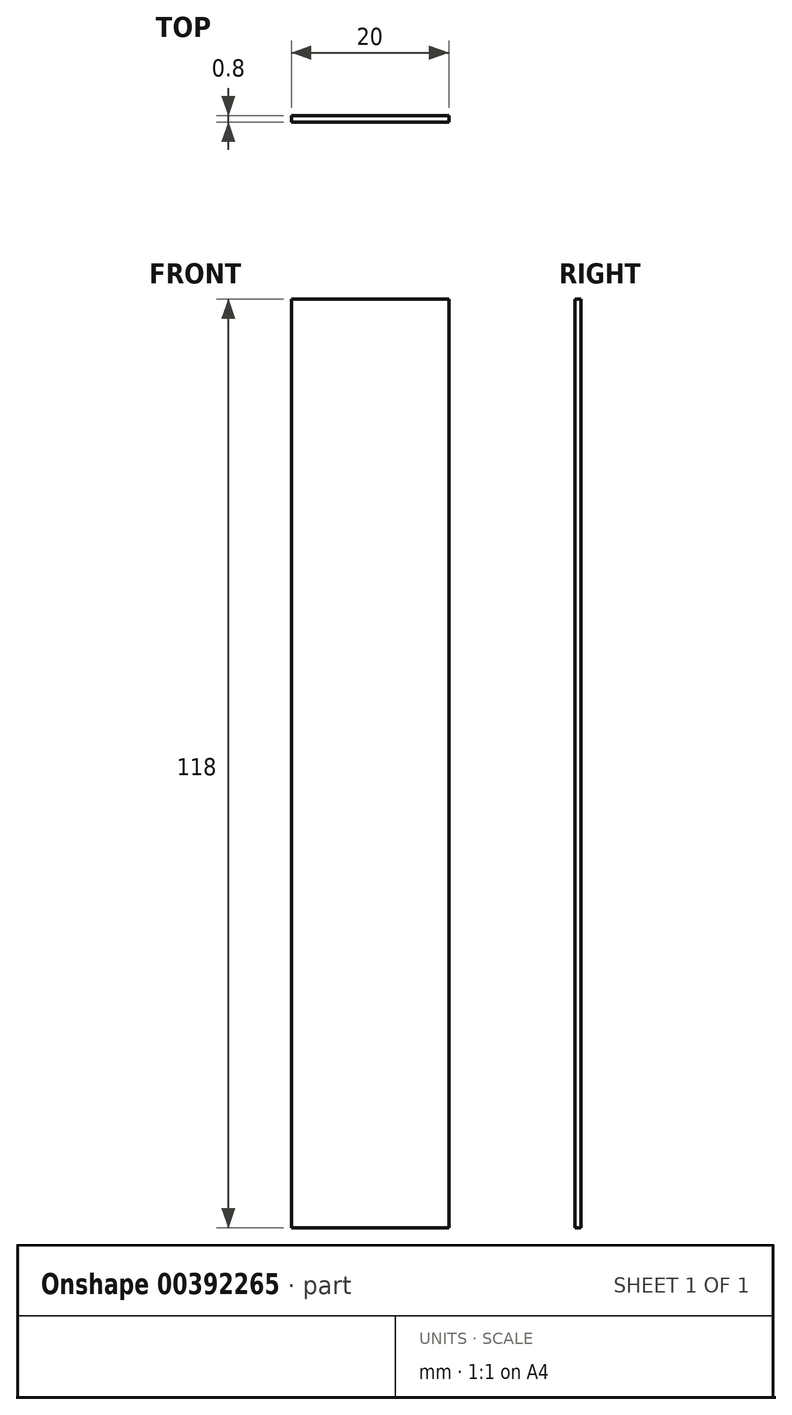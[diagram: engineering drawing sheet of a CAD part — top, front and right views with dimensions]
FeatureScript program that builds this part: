
annotation { "Feature Type Name" : "Feature", "Feature Type Description" : "" }
export const myFeature = defineFeature(function(context is Context, id is Id, definition is map)
    precondition{}
    {
        {
            var Q0;
            Q0=qCreatedBy(makeId("Top.planeOp"),FACE);
            var sketch = newSketch(context, id + "F0", { "sketchPlane" : qUnion([Q0])});
            skLineSegment(sketch, "E0.bottom", {"start": v(10, -0.4) * mm, "end": v(-10, -0.4) * mm});
            skLineSegment(sketch, "E0.top", {"start": v(10, 0.4) * mm, "end": v(-10, 0.4) * mm});
            skLineSegment(sketch, "E0.left", {"start": v(10, -0.4) * mm, "end": v(10, 0.4) * mm});
            skLineSegment(sketch, "E0.right", {"start": v(-10, -0.4) * mm, "end": v(-10, 0.4) * mm});
            skPoint(sketch, "E0.middle", {"position": v(0, 0) * mm});
            skSolve(sketch);
        }
        {
            var Q0;
            Q0 = qSketchRegion(id + "F0", true);
            extrude(context, id + "F1", {"entities" : qUnion([Q0]), "depth" : 118 * mm});
        }
    });
